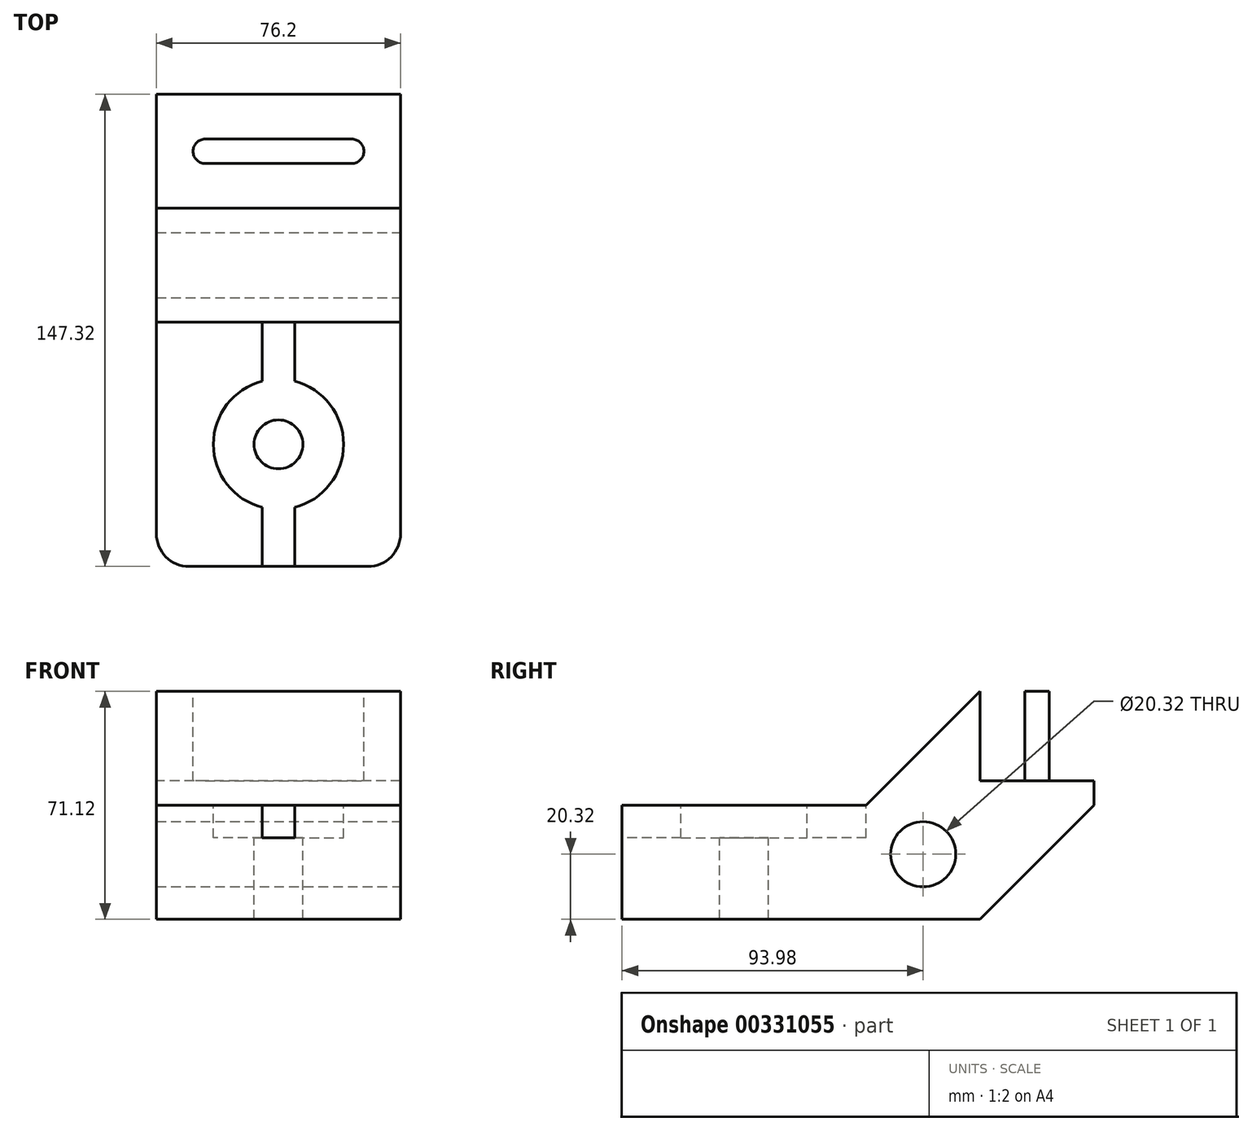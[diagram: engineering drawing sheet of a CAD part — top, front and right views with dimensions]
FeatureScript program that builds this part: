
annotation { "Feature Type Name" : "Feature", "Feature Type Description" : "" }
export const myFeature = defineFeature(function(context is Context, id is Id, definition is map)
    precondition{}
    {
        {
            var Q0;
            Q0=qCreatedBy(makeId("Right.planeOp"),FACE);
            var sketch = newSketch(context, id + "F0", { "sketchPlane" : qUnion([Q0])});
            skLineSegment(sketch, "E0.bottom", {"start": v(-73.66, 71.12) * mm, "end": v(73.66, 71.12) * mm});
            skLineSegment(sketch, "E0.top", {"start": v(-73.66, 0) * mm, "end": v(73.66, 0) * mm});
            skLineSegment(sketch, "E0.left", {"start": v(-73.66, 71.12) * mm, "end": v(-73.66, 0) * mm});
            skLineSegment(sketch, "E0.right", {"start": v(73.66, 71.12) * mm, "end": v(73.66, 0) * mm});
            skSolve(sketch);
        }
        {
            var Q0;
            Q0 = qSketchRegion(id + "F0", true);
            extrude(context, id + "F1", {"entities" : qUnion([Q0]), "endBound" : BoundingType.SYMMETRIC, "depth" : 76.2 * mm});
        }
        {
            var Q0;
            Q0=makeQuery(id+"F1.opExtrude","CAP_FACE",FACE,{"disambiguationData":[OSD([sQuery(id+"F0.wireOp",EDGE,"E0.bottom"),sQuery(id+"F0.wireOp",EDGE,"E0.top"),sQuery(id+"F0.wireOp",EDGE,"E0.left"),sQuery(id+"F0.wireOp",EDGE,"E0.right")])],"isStart":false});
            var sketch = newSketch(context, id + "F2", { "sketchPlane" : qUnion([Q0])});
            skLineSegment(sketch, "E1", {"start": v(38.1, 71.12) * mm, "end": v(2.54, 35.56) * mm});
            skLineSegment(sketch, "E2", {"start": v(2.54, 35.56) * mm, "end": v(-73.66, 35.56) * mm});
            skLineSegment(sketch, "E3", {"start": v(38.1, 71.12) * mm, "end": v(73.66, 71.12) * mm});
            skLineSegment(sketch, "E4", {"start": v(73.66, 71.12) * mm, "end": v(73.66, 35.56) * mm});
            skLineSegment(sketch, "E5", {"start": v(73.66, 35.56) * mm, "end": v(38.1, 0) * mm});
            skLineSegment(sketch, "E6", {"start": v(38.1, 0) * mm, "end": v(-73.66, 0) * mm});
            skLineSegment(sketch, "E7", {"start": v(-73.66, 0) * mm, "end": v(-73.66, 35.56) * mm});
            skSolve(sketch);
        }
        {
            var Q0;
            {var subQ0=sQuery(id+"F2.wireOp",EDGE,"E1");Q0=makeQuery(id+"F2.imprint","IMPRINT",FACE,{"disambiguationData":[TD([[makeQuery(id+"F2.imprint","IMPRINT",EDGE,{"derivedFrom":subQ0}),-1.0]])]});}
            var Q1;
            {var subQ0=sQuery(id+"F2.wireOp",EDGE,"E5");Q1=makeQuery(id+"F2.imprint","IMPRINT",FACE,{"disambiguationData":[TD([[makeQuery(id+"F2.imprint","IMPRINT",EDGE,{"derivedFrom":subQ0}),1.0]])]});}
            extrude(context, id + "F3", {"entities" : qUnion([Q0, Q1]), "operationType" : NewBodyOperationType.REMOVE, "endBound" : BoundingType.THROUGH_ALL, "oppositeDirection" : true, "depth" : 25.4 * mm});
        }
        {
            var Q0;
            Q0=makeQuery(id+"F1.opExtrude","SWEPT_FACE",FACE,{"disambiguationData":[OSD([sQuery(id+"F0.wireOp",EDGE,"E0.bottom")])]});
            var sketch = newSketch(context, id + "F4", { "sketchPlane" : qUnion([Q0])});
            skLineSegment(sketch, "E8", {"start": v(-22.86, 55.88) * mm, "end": v(22.86, 55.88) * mm, "construction": true});
            skArc(sketch, "E9.0.startCap", {"start": v(-22.86, 52.07) * mm, "mid": v(-26.67, 55.88) * mm, "end": v(-22.86, 59.69) * mm});
            skArc(sketch, "E9.0.endCap", {"start": v(22.86, 59.7) * mm, "mid": v(26.67, 55.88) * mm, "end": v(22.86, 52.07) * mm});
            skLineSegment(sketch, "E9.0.left", {"start": v(-22.86, 59.69) * mm, "end": v(22.86, 59.69) * mm});
            skLineSegment(sketch, "E9.0.right", {"start": v(-22.86, 52.07) * mm, "end": v(22.86, 52.07) * mm});
            skSolve(sketch);
        }
        {
            var Q0;
            Q0=makeQuery(id+"F4.imprint","IMPRINT",FACE,{"disambiguationData":[TD([[makeQuery(id+"F4.imprint","IMPRINT",EDGE,{"derivedFrom":sQuery(id+"F4.wireOp",EDGE,"E9.0.startCap")}),-1.0]])]});
            extrude(context, id + "F5", {"entities" : qUnion([Q0]), "operationType" : NewBodyOperationType.REMOVE, "oppositeDirection" : true, "depth" : 27.94 * mm});
        }
        {
            var Q0;
            Q0=makeQuery(id+"F1.opExtrude","CAP_EDGE",EDGE,{"disambiguationData":[OSD([sQuery(id+"F0.wireOp",EDGE,"E0.left")])],"isStart":false});
            var Q1;
            Q1=makeQuery(id+"F1.opExtrude","CAP_EDGE",EDGE,{"disambiguationData":[OSD([sQuery(id+"F0.wireOp",EDGE,"E0.left")])],"isStart":true});
            fillet(context, id + "F6", {"entities" : qUnion([Q0, Q1]), "radius" : 10.16 * mm, "tangentPropagation" : true, "allowEdgeOverflow" : false});
        }
        {
            var Q0;
            Q0=makeQuery(id+"F3.boolean.opBoolean","COPY",FACE,{"derivedFrom":makeQuery(id+"F3.opExtrude","SWEPT_FACE",FACE,{"disambiguationData":[OSD([sQuery(id+"F2.wireOp",EDGE,"E2")])]})});
            var sketch = newSketch(context, id + "F7", { "sketchPlane" : qUnion([Q0])});
            skPoint(sketch, "E10", {"position": v(0, -35.56) * mm});
            skSolve(sketch);
        }
        {
            var Q0;
            Q0=sQuery(id+"F7.wireOp",VERTEX,"E10");
            var Q1;
            Q1=makeQuery(id+"F1.opExtrude","SWEPT_BODY",BODY,{"disambiguationData":[OSD([sQuery(id+"F0.wireOp",EDGE,"E0.bottom"),sQuery(id+"F0.wireOp",EDGE,"E0.top"),sQuery(id+"F0.wireOp",EDGE,"E0.left"),sQuery(id+"F0.wireOp",EDGE,"E0.right")])]});
            hole(context, id + "F8", {"style" : HoleStyle.C_BORE, "endStyle" : HoleEndStyle.THROUGH, "holeDiameter" : 15.24 * mm, "cBoreDiameter" : 40.64 * mm, "cBoreDepth" : 10.16 * mm, "tappedDepth" : 12.7 * mm, "tapClearance" : 3, "locations" : qUnion([Q0]), "scope" : qUnion([Q1])});
        }
        {
            var Q0;
            Q0=makeQuery(id+"F3.boolean.opBoolean","COPY",FACE,{"derivedFrom":makeQuery(id+"F3.opExtrude","SWEPT_FACE",FACE,{"disambiguationData":[OSD([sQuery(id+"F2.wireOp",EDGE,"E2")])]})});
            var sketch = newSketch(context, id + "F9", { "sketchPlane" : qUnion([Q0])});
            skLineSegment(sketch, "E11.bottom", {"start": v(5.08, 2.54) * mm, "end": v(-5.08, 2.54) * mm});
            skLineSegment(sketch, "E11.top", {"start": v(5.08, -73.66) * mm, "end": v(-5.08, -73.66) * mm});
            skLineSegment(sketch, "E11.left", {"start": v(5.08, 2.54) * mm, "end": v(5.08, -73.66) * mm});
            skLineSegment(sketch, "E11.right", {"start": v(-5.08, 2.54) * mm, "end": v(-5.08, -73.66) * mm});
            skSolve(sketch);
        }
        {
            var Q0;
            {var subQ0=sQuery(id+"F9.wireOp",EDGE,"E11.top");Q0=makeQuery(id+"F9.imprint","IMPRINT",FACE,{"disambiguationData":[TD([[makeQuery(id+"F9.imprint","IMPRINT",EDGE,{"derivedFrom":subQ0}),1.0]])]});}
            var Q1;
            {var subQ0=sQuery(id+"F9.wireOp",EDGE,"E11.bottom");Q1=makeQuery(id+"F9.imprint","IMPRINT",FACE,{"disambiguationData":[TD([[makeQuery(id+"F9.imprint","IMPRINT",EDGE,{"derivedFrom":subQ0}),-1.0]])]});}
            extrude(context, id + "F10", {"entities" : qUnion([Q0, Q1]), "operationType" : NewBodyOperationType.REMOVE, "oppositeDirection" : true, "depth" : 10.16 * mm});
        }
        {
            var Q0;
            Q0=makeQuery(id+"F1.opExtrude","CAP_FACE",FACE,{"disambiguationData":[OSD([sQuery(id+"F0.wireOp",EDGE,"E0.bottom"),sQuery(id+"F0.wireOp",EDGE,"E0.top"),sQuery(id+"F0.wireOp",EDGE,"E0.left"),sQuery(id+"F0.wireOp",EDGE,"E0.right")])],"isStart":false});
            var sketch = newSketch(context, id + "F11", { "sketchPlane" : qUnion([Q0])});
            skPoint(sketch, "E12", {"position": v(20.32, 20.32) * mm});
            skSolve(sketch);
        }
        {
            var Q0;
            Q0=sQuery(id+"F11.wireOp",VERTEX,"E12");
            var Q1;
            Q1=makeQuery(id+"F1.opExtrude","SWEPT_BODY",BODY,{"disambiguationData":[OSD([sQuery(id+"F0.wireOp",EDGE,"E0.bottom"),sQuery(id+"F0.wireOp",EDGE,"E0.top"),sQuery(id+"F0.wireOp",EDGE,"E0.left"),sQuery(id+"F0.wireOp",EDGE,"E0.right")])]});
            hole(context, id + "F12", {"style" : HoleStyle.SIMPLE, "endStyle" : HoleEndStyle.THROUGH, "holeDiameter" : 20.32 * mm, "tappedDepth" : 12.7 * mm, "tapClearance" : 3, "locations" : qUnion([Q0]), "scope" : qUnion([Q1])});
        }
    });
